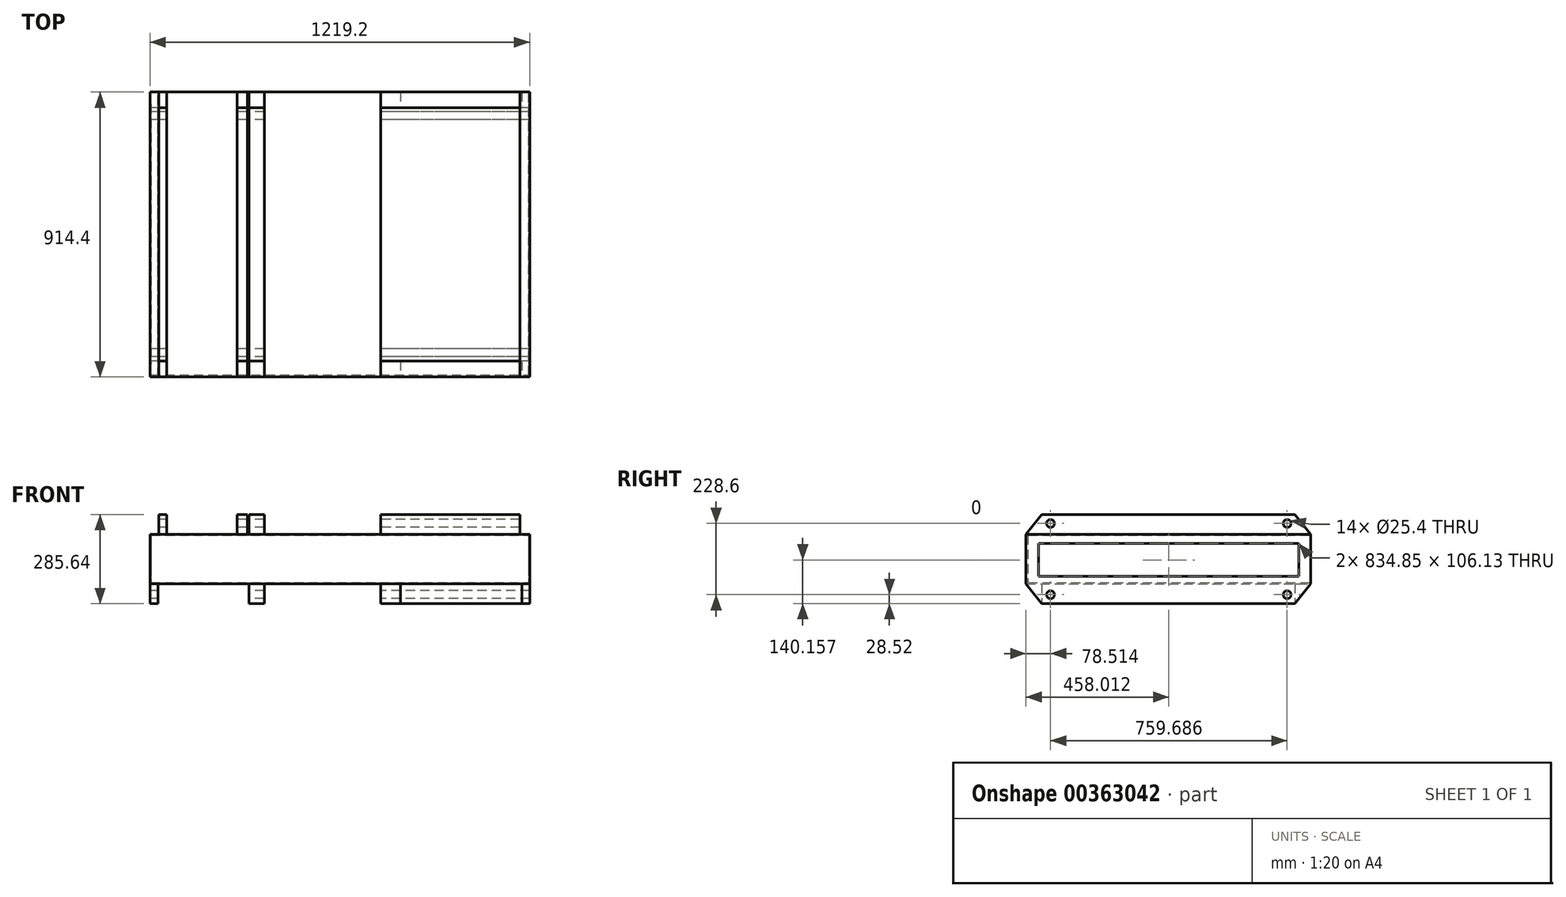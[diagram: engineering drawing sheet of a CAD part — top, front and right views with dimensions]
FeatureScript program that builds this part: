
annotation { "Feature Type Name" : "Feature", "Feature Type Description" : "" }
export const myFeature = defineFeature(function(context is Context, id is Id, definition is map)
    precondition{}
    {
        {
            var Q0;
            Q0=qCreatedBy(makeId("Right.planeOp"),FACE);
            var sketch = newSketch(context, id + "F0", { "sketchPlane" : qUnion([Q0])});
            skLineSegment(sketch, "E0.bottom", {"start": v(457.2, 79.37) * mm, "end": v(-457.2, 79.37) * mm});
            skLineSegment(sketch, "E0.top", {"start": v(457.2, -79.37) * mm, "end": v(-457.2, -79.38) * mm});
            skLineSegment(sketch, "E0.left", {"start": v(457.2, 79.37) * mm, "end": v(457.2, -79.37) * mm});
            skLineSegment(sketch, "E0.right", {"start": v(-457.2, 79.37) * mm, "end": v(-457.2, -79.38) * mm});
            skPoint(sketch, "E0.middle", {"position": v(0, 0) * mm});
            skLineSegment(sketch, "E1", {"start": v(457.2, 79.38) * mm, "end": v(406.4, 142.82) * mm});
            skLineSegment(sketch, "E2", {"start": v(406.4, 142.82) * mm, "end": v(-406.4, 142.82) * mm});
            skLineSegment(sketch, "E3", {"start": v(-406.4, 142.82) * mm, "end": v(-457.2, 79.37) * mm});
            skLineSegment(sketch, "E4", {"start": v(-457.2, -79.38) * mm, "end": v(-406.4, -142.82) * mm});
            skLineSegment(sketch, "E5", {"start": v(-406.4, -142.82) * mm, "end": v(406.4, -142.82) * mm});
            skLineSegment(sketch, "E6", {"start": v(406.4, -142.82) * mm, "end": v(457.2, -79.37) * mm});
            skPoint(sketch, "E7", {"position": v(381, 114.3) * mm});
            skPoint(sketch, "E8", {"position": v(-378.69, 114.3) * mm});
            skPoint(sketch, "E9", {"position": v(381, -114.3) * mm});
            skPoint(sketch, "E10", {"position": v(-378.69, -114.3) * mm});
            skLineSegment(sketch, "E11.bottom", {"start": v(418.24, 50.4) * mm, "end": v(-416.61, 50.4) * mm});
            skLineSegment(sketch, "E11.top", {"start": v(418.24, -55.73) * mm, "end": v(-416.61, -55.73) * mm});
            skLineSegment(sketch, "E11.left", {"start": v(418.24, 50.4) * mm, "end": v(418.24, -55.73) * mm});
            skLineSegment(sketch, "E11.right", {"start": v(-416.61, 50.4) * mm, "end": v(-416.61, -55.73) * mm});
            skSolve(sketch);
        }
        {
            var Q0;
            {var subQ0=sQuery(id+"F0.wireOp",EDGE,"E0.right");Q0=makeQuery(id+"F0.imprint","IMPRINT",FACE,{"disambiguationData":[TD([[makeQuery(id+"F0.imprint","IMPRINT",EDGE,{"derivedFrom":subQ0}),1.0]])]});}
            var Q1;
            {var subQ0=sQuery(id+"F0.wireOp",EDGE,"E0.left");Q1=makeQuery(id+"F0.imprint","IMPRINT",FACE,{"disambiguationData":[TD([[makeQuery(id+"F0.imprint","IMPRINT",EDGE,{"derivedFrom":subQ0}),-1.0]])]});}
            extrude(context, id + "F1", {"entities" : qUnion([Q0, Q1]), "depth" : 1219.2 * mm});
        }
        {
            var Q0;
            {var subQ0=sQuery(id+"F0.wireOp",EDGE,"E1");Q0=makeQuery(id+"F0.imprint","IMPRINT",FACE,{"disambiguationData":[TD([[makeQuery(id+"F0.imprint","IMPRINT",EDGE,{"derivedFrom":subQ0}),1.0]])]});}
            extrude(context, id + "F2", {"entities" : qUnion([Q0]), "operationType" : NewBodyOperationType.ADD, "depth" : 25.4 * mm});
        }
        {
            var Q0;
            {var subQ0=sQuery(id+"F0.wireOp",EDGE,"E4");Q0=makeQuery(id+"F0.imprint","IMPRINT",FACE,{"disambiguationData":[TD([[makeQuery(id+"F0.imprint","IMPRINT",EDGE,{"derivedFrom":subQ0}),1.0]])]});}
            extrude(context, id + "F3", {"entities" : qUnion([Q0]), "operationType" : NewBodyOperationType.ADD, "depth" : 25.4 * mm});
        }
        {
            var Q0;
            Q0=makeQuery(id+"F0.imprint","IMPRINT",FACE,{"disambiguationData":[TD([[makeQuery(id+"F0.imprint","IMPRINT",EDGE,{"derivedFrom":sQuery(id+"F0.wireOp",EDGE,"E0.bottom")}),-1.0]])]});
            extrude(context, id + "F4", {"entities" : qUnion([Q0]), "operationType" : NewBodyOperationType.ADD, "depth" : 1219.2 * mm});
        }
        {
            var Q0;
            Q0=makeQuery(id+"F0.imprint","IMPRINT",FACE,{"disambiguationData":[TD([[makeQuery(id+"F0.imprint","IMPRINT",EDGE,{"derivedFrom":sQuery(id+"F0.wireOp",EDGE,"E0.top")}),1.0]])]});
            extrude(context, id + "F5", {"entities" : qUnion([Q0]), "operationType" : NewBodyOperationType.ADD, "depth" : 1219.2 * mm});
        }
        {
            var Q0;
            Q0=sQuery(id+"F0.wireOp",VERTEX,"E8");
            var Q1;
            Q1=sQuery(id+"F0.wireOp",VERTEX,"E9");
            var Q2;
            Q2=sQuery(id+"F0.wireOp",VERTEX,"E10");
            var Q3;
            Q3=sQuery(id+"F0.wireOp",VERTEX,"E7");
            var Q4;
            Q4=makeQuery(id+"F1.opExtrude","SWEPT_BODY",BODY,{"disambiguationData":[OSD([sQuery(id+"F0.wireOp",EDGE,"E0.bottom"),sQuery(id+"F0.wireOp",EDGE,"E0.top"),sQuery(id+"F0.wireOp",EDGE,"E0.left"),sQuery(id+"F0.wireOp",EDGE,"E0.right")])]});
            hole(context, id + "F6", {"style" : HoleStyle.SIMPLE, "endStyle" : HoleEndStyle.THROUGH, "oppositeDirection" : true, "holeDiameter" : 25.4 * mm, "isTappedThrough" : true, "tappedDepth" : 12.7 * mm, "tapClearance" : 3, "startFromSketch" : true, "locations" : qUnion([Q0, Q1, Q2, Q3]), "scope" : qUnion([Q4])});
        }
        {
            var Q0;
            {var subQ0=sQuery(id+"F0.wireOp",EDGE,"E5");Q0=makeQuery(id+"F5.boolean.opBoolean","MERGE",FACE,{"derivedFrom":[makeQuery(id+"F3.opExtrude","SWEPT_FACE",FACE,{"disambiguationData":[OSD([subQ0])]}),makeQuery(id+"F5.opExtrude","SWEPT_FACE",FACE,{"disambiguationData":[OSD([subQ0])]})]});}
            var sketch = newSketch(context, id + "F7", { "sketchPlane" : qUnion([Q0])});
            skLineSegment(sketch, "E12.bottom", {"start": v(25.4, 551.74) * mm, "end": v(1193.8, 551.74) * mm});
            skLineSegment(sketch, "E12.top", {"start": v(25.4, -593.28) * mm, "end": v(1193.8, -593.28) * mm});
            skLineSegment(sketch, "E12.left", {"start": v(25.4, 551.74) * mm, "end": v(25.4, -593.28) * mm});
            skLineSegment(sketch, "E12.right", {"start": v(1193.8, 551.74) * mm, "end": v(1193.8, -593.28) * mm});
            skLineSegment(sketch, "E13.bottom", {"start": v(1219.2, 23.88) * mm, "end": v(1193.8, 23.88) * mm});
            skLineSegment(sketch, "E13.top", {"start": v(1219.2, -593.28) * mm, "end": v(1193.8, -593.28) * mm});
            skLineSegment(sketch, "E13.left", {"start": v(1219.2, 23.88) * mm, "end": v(1219.2, -593.28) * mm});
            skLineSegment(sketch, "E13.right", {"start": v(1193.8, 23.88) * mm, "end": v(1193.8, -593.28) * mm});
            skLineSegment(sketch, "E14.top", {"start": v(1219.2, 551.74) * mm, "end": v(1193.8, 551.74) * mm});
            skLineSegment(sketch, "E14.left", {"start": v(1219.2, 23.88) * mm, "end": v(1219.2, 551.74) * mm});
            skLineSegment(sketch, "E14.right", {"start": v(1193.8, 23.88) * mm, "end": v(1193.8, 551.74) * mm});
            skPoint(sketch, "E15.oppositeSnap0", {"position": v(0, 0) * mm});
            skLineSegment(sketch, "E15.bottom", {"start": v(25.4, 551.74) * mm, "end": v(0, 551.74) * mm});
            skLineSegment(sketch, "E15.top", {"start": v(25.4, -593.28) * mm, "end": v(0, -593.28) * mm});
            skLineSegment(sketch, "E15.right", {"start": v(0, 551.74) * mm, "end": v(0, -593.28) * mm});
            skLineSegment(sketch, "E16.bottom", {"start": v(318.15, 551.74) * mm, "end": v(367.07, 551.74) * mm});
            skLineSegment(sketch, "E16.top", {"start": v(318.15, -593.28) * mm, "end": v(367.07, -593.28) * mm});
            skLineSegment(sketch, "E16.left", {"start": v(318.15, 551.74) * mm, "end": v(318.15, -593.28) * mm});
            skLineSegment(sketch, "E16.right", {"start": v(367.07, 551.74) * mm, "end": v(367.07, -593.28) * mm});
            skLineSegment(sketch, "E17.bottom", {"start": v(740.44, 551.74) * mm, "end": v(804.81, 551.74) * mm});
            skLineSegment(sketch, "E17.top", {"start": v(740.44, -593.28) * mm, "end": v(804.81, -593.28) * mm});
            skLineSegment(sketch, "E17.left", {"start": v(740.44, 551.74) * mm, "end": v(740.44, -593.28) * mm});
            skLineSegment(sketch, "E17.right", {"start": v(804.81, 551.74) * mm, "end": v(804.81, -593.28) * mm});
            skSolve(sketch);
        }
        {
            var Q0;
            {var subQ0=sQuery(id+"F7.wireOp",EDGE,"E14.right");var subQ7=sQuery(id+"F7.wireOp",EDGE,"E13.right");var subQ8=makeQuery(id+"F7.imprint","INTERSECT",VERTEX,{"derivedFrom":[subQ7,sQuery(id+"F7.wireOp",EDGE,"E13.bottom"),subQ0]});Q0=makeQuery(id+"F7.imprint","IMPRINT",FACE,{"disambiguationData":[TD([[makeQuery(id+"F7.imprint","IMPRINT",EDGE,{"disambiguationData":[TD([[subQ8,-1.0]])],"derivedFrom":subQ7}),-1.0]])]});}
            var Q1;
            {var subQ0=sQuery(id+"F7.wireOp",EDGE,"E13.right");var subQ1=sQuery(id+"F7.wireOp",EDGE,"E12.top");var subQ2=makeQuery(id+"F7.imprint","INTERSECT",VERTEX,{"derivedFrom":[subQ1,sQuery(id+"F7.wireOp",EDGE,"E13.top"),subQ0]});Q1=makeQuery(id+"F7.imprint","IMPRINT",FACE,{"disambiguationData":[TD([[makeQuery(id+"F7.imprint","IMPRINT",EDGE,{"disambiguationData":[TD([[subQ2,1.0]])],"derivedFrom":subQ1}),1.0]])]});}
            var Q2;
            {var subQ0=sQuery(id+"F7.wireOp",EDGE,"E16.right");var subQ1=sQuery(id+"F7.wireOp",EDGE,"E12.top");var subQ2=makeQuery(id+"F7.imprint","INTERSECT",VERTEX,{"derivedFrom":[subQ1,sQuery(id+"F7.wireOp",EDGE,"E16.top"),subQ0]});Q2=makeQuery(id+"F7.imprint","IMPRINT",FACE,{"disambiguationData":[TD([[makeQuery(id+"F7.imprint","IMPRINT",EDGE,{"disambiguationData":[TD([[subQ2,-1.0]])],"derivedFrom":subQ1}),1.0]])]});}
            var Q3;
            {var subQ0=sQuery(id+"F7.wireOp",EDGE,"E16.right");var subQ1=sQuery(id+"F0.wireOp",EDGE,"E5");var subQ2=sQuery(id+"F0.wireOp",EDGE,"E4");var subQ3=makeQuery(id+"F5.boolean.opBoolean","MERGE",EDGE,{"derivedFrom":[makeQuery(id+"F3.opExtrude","SWEPT_EDGE",EDGE,{"disambiguationData":[OSD([subQ2,subQ1])]}),makeQuery(id+"F5.opExtrude","SWEPT_EDGE",EDGE,{"disambiguationData":[OSD([subQ2,subQ1])]})]});var subQ4=makeQuery(id+"F7.imprint","INTERSECT",VERTEX,{"derivedFrom":[subQ3,subQ0]});Q3=makeQuery(id+"F7.imprint","IMPRINT",FACE,{"disambiguationData":[TD([[makeQuery(id+"F7.imprint","IMPRINT",EDGE,{"disambiguationData":[TD([[subQ4,-1.0]])],"derivedFrom":subQ0}),1.0]])]});}
            var Q4;
            {var subQ0=sQuery(id+"F7.wireOp",EDGE,"E12.left");var subQ1=sQuery(id+"F0.wireOp",EDGE,"E5");var subQ2=sQuery(id+"F0.wireOp",EDGE,"E4");var subQ3=makeQuery(id+"F5.boolean.opBoolean","MERGE",EDGE,{"derivedFrom":[makeQuery(id+"F3.opExtrude","SWEPT_EDGE",EDGE,{"disambiguationData":[OSD([subQ2,subQ1])]}),makeQuery(id+"F5.opExtrude","SWEPT_EDGE",EDGE,{"disambiguationData":[OSD([subQ2,subQ1])]})]});var subQ4=makeQuery(id+"F7.imprint","INTERSECT",VERTEX,{"derivedFrom":[subQ3,subQ0]});Q4=makeQuery(id+"F7.imprint","IMPRINT",FACE,{"disambiguationData":[TD([[makeQuery(id+"F7.imprint","IMPRINT",EDGE,{"disambiguationData":[TD([[subQ4,-1.0]])],"derivedFrom":subQ0}),1.0]])]});}
            var Q5;
            {var subQ0=sQuery(id+"F7.wireOp",EDGE,"E12.left");var subQ1=sQuery(id+"F7.wireOp",EDGE,"E12.top");var subQ2=makeQuery(id+"F7.imprint","INTERSECT",VERTEX,{"derivedFrom":[subQ1,sQuery(id+"F7.wireOp",EDGE,"E15.top"),subQ0]});Q5=makeQuery(id+"F7.imprint","IMPRINT",FACE,{"disambiguationData":[TD([[makeQuery(id+"F7.imprint","IMPRINT",EDGE,{"disambiguationData":[TD([[subQ2,-1.0]])],"derivedFrom":subQ1}),1.0]])]});}
            var Q6;
            {var subQ0=sQuery(id+"F7.wireOp",EDGE,"E14.right");var subQ1=sQuery(id+"F7.wireOp",EDGE,"E12.bottom");var subQ2=makeQuery(id+"F7.imprint","INTERSECT",VERTEX,{"derivedFrom":[subQ1,sQuery(id+"F7.wireOp",EDGE,"E14.top"),subQ0]});Q6=makeQuery(id+"F7.imprint","IMPRINT",FACE,{"disambiguationData":[TD([[makeQuery(id+"F7.imprint","IMPRINT",EDGE,{"disambiguationData":[TD([[subQ2,1.0]])],"derivedFrom":subQ1}),-1.0]])]});}
            var Q7;
            {var subQ0=sQuery(id+"F7.wireOp",EDGE,"E16.right");var subQ1=sQuery(id+"F7.wireOp",EDGE,"E12.bottom");var subQ2=makeQuery(id+"F7.imprint","INTERSECT",VERTEX,{"derivedFrom":[subQ1,sQuery(id+"F7.wireOp",EDGE,"E16.bottom"),subQ0]});Q7=makeQuery(id+"F7.imprint","IMPRINT",FACE,{"disambiguationData":[TD([[makeQuery(id+"F7.imprint","IMPRINT",EDGE,{"disambiguationData":[TD([[subQ2,-1.0]])],"derivedFrom":subQ1}),-1.0]])]});}
            var Q8;
            {var subQ0=sQuery(id+"F7.wireOp",EDGE,"E12.left");var subQ1=sQuery(id+"F7.wireOp",EDGE,"E12.bottom");var subQ2=makeQuery(id+"F7.imprint","INTERSECT",VERTEX,{"derivedFrom":[subQ1,sQuery(id+"F7.wireOp",EDGE,"E15.bottom"),subQ0]});Q8=makeQuery(id+"F7.imprint","IMPRINT",FACE,{"disambiguationData":[TD([[makeQuery(id+"F7.imprint","IMPRINT",EDGE,{"disambiguationData":[TD([[subQ2,-1.0]])],"derivedFrom":subQ1}),-1.0]])]});}
            extrude(context, id + "F8", {"entities" : qUnion([Q0, Q1, Q2, Q3, Q4, Q5, Q6, Q7, Q8]), "operationType" : NewBodyOperationType.REMOVE, "oppositeDirection" : true, "depth" : 63.5 * mm});
        }
        {
            var Q0;
            Q0=makeQuery(id+"F1.opExtrude","SWEPT_FACE",FACE,{"disambiguationData":[OSD([sQuery(id+"F0.wireOp",EDGE,"E0.left")])]});
            var sketch = newSketch(context, id + "F9", { "sketchPlane" : qUnion([Q0])});
            skLineSegment(sketch, "E18.bottom", {"start": v(-1219.2, 79.37) * mm, "end": v(0, 79.37) * mm});
            skLineSegment(sketch, "E18.top", {"start": v(-1219.2, -79.38) * mm, "end": v(0, -79.38) * mm});
            skLineSegment(sketch, "E18.left", {"start": v(-1219.2, 79.37) * mm, "end": v(-1219.2, -79.38) * mm});
            skLineSegment(sketch, "E18.right", {"start": v(0, 79.37) * mm, "end": v(0, -79.38) * mm});
            skLineSegment(sketch, "E19.bottom", {"start": v(11.99, 76.2) * mm, "end": v(-1241.76, 76.2) * mm});
            skLineSegment(sketch, "E19.top", {"start": v(11.99, -76.2) * mm, "end": v(-1241.76, -76.2) * mm});
            skLineSegment(sketch, "E19.left", {"start": v(11.99, 76.2) * mm, "end": v(11.99, -76.2) * mm});
            skLineSegment(sketch, "E19.right", {"start": v(-1241.76, 76.2) * mm, "end": v(-1241.76, -76.2) * mm});
            skLineSegment(sketch, "E20.bottom", {"start": v(-1247.32, -79.38) * mm, "end": v(48.41, -79.38) * mm});
            skLineSegment(sketch, "E20.top", {"start": v(-1247.32, 79.37) * mm, "end": v(48.41, 79.37) * mm});
            skLineSegment(sketch, "E20.left", {"start": v(-1247.32, -79.38) * mm, "end": v(-1247.32, 79.37) * mm});
            skLineSegment(sketch, "E20.right", {"start": v(48.41, -79.38) * mm, "end": v(48.41, 79.37) * mm});
            skLineSegment(sketch, "E21.bottom", {"start": v(11.99, 76.2) * mm, "end": v(0, 76.2) * mm});
            skLineSegment(sketch, "E21.top", {"start": v(11.99, 89.74) * mm, "end": v(0, 89.74) * mm});
            skLineSegment(sketch, "E21.left", {"start": v(11.99, 76.2) * mm, "end": v(11.99, 89.74) * mm});
            skLineSegment(sketch, "E21.right", {"start": v(0, 76.2) * mm, "end": v(0, 89.74) * mm});
            skLineSegment(sketch, "E22.bottom", {"start": v(11.99, -76.2) * mm, "end": v(48.41, -76.2) * mm});
            skLineSegment(sketch, "E22.top", {"start": v(11.99, -79.38) * mm, "end": v(48.41, -79.38) * mm});
            skLineSegment(sketch, "E22.left", {"start": v(11.99, -76.2) * mm, "end": v(11.99, -79.38) * mm});
            skLineSegment(sketch, "E22.right", {"start": v(48.41, -76.2) * mm, "end": v(48.41, -79.38) * mm});
            skLineSegment(sketch, "E23.bottom", {"start": v(0, 76.2) * mm, "end": v(-3.18, 76.2) * mm});
            skLineSegment(sketch, "E23.top", {"start": v(0, -76.2) * mm, "end": v(-3.17, -76.2) * mm});
            skLineSegment(sketch, "E23.left", {"start": v(0, 76.2) * mm, "end": v(0, -76.2) * mm});
            skLineSegment(sketch, "E23.right", {"start": v(-3.18, 76.2) * mm, "end": v(-3.17, -76.2) * mm});
            skLineSegment(sketch, "E24.bottom", {"start": v(-1219.2, 76.2) * mm, "end": v(-1216.03, 76.2) * mm});
            skLineSegment(sketch, "E24.top", {"start": v(-1219.2, -76.2) * mm, "end": v(-1216.03, -76.2) * mm});
            skLineSegment(sketch, "E24.left", {"start": v(-1219.2, 76.2) * mm, "end": v(-1219.2, -76.2) * mm});
            skLineSegment(sketch, "E24.right", {"start": v(-1216.03, 76.2) * mm, "end": v(-1216.03, -76.2) * mm});
            skLineSegment(sketch, "E25.bottom", {"start": v(0, 79.37) * mm, "end": v(-3.18, 79.37) * mm});
            skLineSegment(sketch, "E25.left", {"start": v(0, 79.37) * mm, "end": v(0, 76.2) * mm});
            skLineSegment(sketch, "E25.right", {"start": v(-3.18, 79.37) * mm, "end": v(-3.18, 76.2) * mm});
            skSolve(sketch);
        }
        {
            var Q0;
            {var subQ0=sQuery(id+"F9.wireOp",EDGE,"E23.right");Q0=makeQuery(id+"F9.imprint","IMPRINT",FACE,{"disambiguationData":[TD([[makeQuery(id+"F9.imprint","IMPRINT",EDGE,{"derivedFrom":subQ0}),-1.0]])]});}
            extrude(context, id + "F10", {"entities" : qUnion([Q0]), "operationType" : NewBodyOperationType.REMOVE, "oppositeDirection" : true, "depth" : 908.05 * mm});
        }
        {
            var Q0;
            {var subQ0=sQuery(id+"F9.wireOp",EDGE,"E23.right");Q0=makeQuery(id+"F9.imprint","IMPRINT",FACE,{"disambiguationData":[TD([[makeQuery(id+"F9.imprint","IMPRINT",EDGE,{"derivedFrom":subQ0}),-1.0]])]});}
            extrude(context, id + "F11", {"entities" : qUnion([Q0]), "operationType" : NewBodyOperationType.REMOVE, "oppositeDirection" : true, "depth" : 889 * mm});
        }
        {
            var Q0;
            Q0=makeQuery(id+"F1.opExtrude","SWEPT_FACE",FACE,{"disambiguationData":[OSD([sQuery(id+"F0.wireOp",EDGE,"E0.right")])]});
            var sketch = newSketch(context, id + "F12", { "sketchPlane" : qUnion([Q0])});
            skLineSegment(sketch, "E26", {"start": v(28.57, 79.37) * mm, "end": v(28.57, 142.31) * mm});
            skLineSegment(sketch, "E27.bottom", {"start": v(28.58, 79.37) * mm, "end": v(279.4, 79.37) * mm});
            skLineSegment(sketch, "E27.top", {"start": v(28.57, 145.91) * mm, "end": v(279.4, 145.91) * mm});
            skLineSegment(sketch, "E27.left", {"start": v(28.58, 79.37) * mm, "end": v(28.57, 145.91) * mm});
            skLineSegment(sketch, "E27.right", {"start": v(279.4, 79.37) * mm, "end": v(279.4, 145.91) * mm});
            skLineSegment(sketch, "E28.top", {"start": v(322.89, 79.37) * mm, "end": v(325.77, 79.37) * mm});
            skLineSegment(sketch, "E29.bottom", {"start": v(318.15, -79.32) * mm, "end": v(367.46, -79.32) * mm});
            skLineSegment(sketch, "E29.top", {"start": v(318.15, 186.17) * mm, "end": v(367.46, 186.17) * mm});
            skLineSegment(sketch, "E29.left", {"start": v(318.15, -79.32) * mm, "end": v(318.15, 186.17) * mm});
            skLineSegment(sketch, "E29.right", {"start": v(367.46, -79.32) * mm, "end": v(367.46, 186.17) * mm});
            skLineSegment(sketch, "E30.bottom", {"start": v(740.44, -79.32) * mm, "end": v(804.81, -79.32) * mm});
            skLineSegment(sketch, "E30.top", {"start": v(740.44, 186.17) * mm, "end": v(804.81, 186.17) * mm});
            skLineSegment(sketch, "E30.left", {"start": v(740.44, -79.32) * mm, "end": v(740.44, 186.17) * mm});
            skLineSegment(sketch, "E30.right", {"start": v(804.81, -79.32) * mm, "end": v(804.81, 186.17) * mm});
            skLineSegment(sketch, "E31.bottom", {"start": v(313.2, 145.91) * mm, "end": v(370.35, 145.91) * mm});
            skLineSegment(sketch, "E31.top", {"start": v(313.2, 79.37) * mm, "end": v(370.35, 79.37) * mm});
            skLineSegment(sketch, "E31.left", {"start": v(313.2, 145.91) * mm, "end": v(313.2, 79.37) * mm});
            skLineSegment(sketch, "E31.right", {"start": v(370.35, 145.91) * mm, "end": v(370.35, 79.37) * mm});
            skLineSegment(sketch, "E32.bottom", {"start": v(740.44, 79.38) * mm, "end": v(736.5, 79.38) * mm});
            skLineSegment(sketch, "E32.top", {"start": v(740.44, 201.6) * mm, "end": v(736.5, 201.6) * mm});
            skLineSegment(sketch, "E32.left", {"start": v(740.44, 79.38) * mm, "end": v(740.44, 201.6) * mm});
            skLineSegment(sketch, "E32.right", {"start": v(736.5, 79.38) * mm, "end": v(736.5, 201.6) * mm});
            skLineSegment(sketch, "E33.bottom", {"start": v(804.81, 79.37) * mm, "end": v(1160.9, 79.37) * mm});
            skLineSegment(sketch, "E33.top", {"start": v(804.81, 167.9) * mm, "end": v(1160.9, 167.9) * mm});
            skLineSegment(sketch, "E33.left", {"start": v(804.81, 79.37) * mm, "end": v(804.81, 167.9) * mm});
            skLineSegment(sketch, "E33.right", {"start": v(1160.9, 79.37) * mm, "end": v(1160.9, 167.9) * mm});
            skLineSegment(sketch, "E34.bottom", {"start": v(1219.2, 167.9) * mm, "end": v(1187.45, 167.9) * mm});
            skLineSegment(sketch, "E34.top", {"start": v(1219.2, 79.37) * mm, "end": v(1187.45, 79.37) * mm});
            skLineSegment(sketch, "E34.left", {"start": v(1219.2, 167.9) * mm, "end": v(1219.2, 79.37) * mm});
            skLineSegment(sketch, "E34.right", {"start": v(1187.45, 167.9) * mm, "end": v(1187.45, 79.37) * mm});
            skLineSegment(sketch, "E35.bottom", {"start": v(1187.45, 167.9) * mm, "end": v(1160.9, 167.9) * mm});
            skLineSegment(sketch, "E35.top", {"start": v(1187.45, 79.37) * mm, "end": v(1160.9, 79.37) * mm});
            skLineSegment(sketch, "E35.right", {"start": v(1160.9, 167.9) * mm, "end": v(1160.9, 79.37) * mm});
            skLineSegment(sketch, "E36.bottom", {"start": v(809.73, 79.37) * mm, "end": v(835.13, 79.37) * mm});
            skLineSegment(sketch, "E36.top", {"start": v(809.73, 159.77) * mm, "end": v(835.13, 159.77) * mm});
            skLineSegment(sketch, "E36.left", {"start": v(809.73, 79.37) * mm, "end": v(809.73, 159.77) * mm});
            skLineSegment(sketch, "E36.right", {"start": v(835.13, 79.37) * mm, "end": v(835.13, 159.77) * mm});
            skPoint(sketch, "E37.oppositeSnap0", {"position": v(772.62, 186.17) * mm});
            skLineSegment(sketch, "E37.bottom", {"start": v(313.2, 79.37) * mm, "end": v(809.6, 79.37) * mm});
            skLineSegment(sketch, "E37.top", {"start": v(313.2, 186.17) * mm, "end": v(809.6, 186.17) * mm});
            skLineSegment(sketch, "E37.left", {"start": v(313.2, 79.37) * mm, "end": v(313.2, 186.17) * mm});
            skLineSegment(sketch, "E37.right", {"start": v(809.6, 79.37) * mm, "end": v(809.6, 186.17) * mm});
            skLineSegment(sketch, "E38.bottom", {"start": v(28.57, 145.91) * mm, "end": v(0, 145.91) * mm});
            skLineSegment(sketch, "E38.top", {"start": v(28.58, 79.37) * mm, "end": v(0, 79.37) * mm});
            skLineSegment(sketch, "E38.left", {"start": v(28.57, 145.91) * mm, "end": v(28.58, 79.37) * mm});
            skLineSegment(sketch, "E38.right", {"start": v(0, 145.91) * mm, "end": v(0, 79.37) * mm});
            skLineSegment(sketch, "E39.bottom", {"start": v(53.97, 145.91) * mm, "end": v(28.57, 145.91) * mm});
            skLineSegment(sketch, "E39.top", {"start": v(53.98, 79.37) * mm, "end": v(28.58, 79.37) * mm});
            skLineSegment(sketch, "E39.left", {"start": v(53.97, 145.91) * mm, "end": v(53.98, 79.37) * mm});
            skSolve(sketch);
        }
        {
            var Q0;
            {var subQ0=sQuery(id+"F12.wireOp",EDGE,"E35.right");Q0=makeQuery(id+"F12.imprint","IMPRINT",FACE,{"disambiguationData":[TD([[makeQuery(id+"F12.imprint","IMPRINT",EDGE,{"derivedFrom":subQ0}),-1.0]])]});}
            var Q1;
            {var subQ0=sQuery(id+"F12.wireOp",EDGE,"E33.left");Q1=makeQuery(id+"F12.imprint","IMPRINT",FACE,{"disambiguationData":[TD([[makeQuery(id+"F12.imprint","IMPRINT",EDGE,{"derivedFrom":subQ0}),-1.0]])]});}
            var Q2;
            {var subQ3=sQuery(id+"F12.wireOp",EDGE,"E33.left");Q2=makeQuery(id+"F12.imprint","IMPRINT",FACE,{"disambiguationData":[TD([[makeQuery(id+"F12.imprint","IMPRINT",EDGE,{"derivedFrom":subQ3}),1.0]])]});}
            var Q3;
            {var subQ0=sQuery(id+"F12.wireOp",EDGE,"E37.bottom");var subQ5=sQuery(id+"F12.wireOp",EDGE,"E32.right");var subQ6=makeQuery(id+"F12.imprint","INTERSECT",VERTEX,{"derivedFrom":[subQ5,subQ0]});Q3=makeQuery(id+"F12.imprint","IMPRINT",FACE,{"disambiguationData":[TD([[makeQuery(id+"F12.imprint","IMPRINT",EDGE,{"disambiguationData":[TD([[subQ6,-1.0]])],"derivedFrom":subQ5}),-1.0]])]});}
            var Q4;
            {var subQ0=sQuery(id+"F12.wireOp",EDGE,"E37.bottom");var subQ1=makeQuery(id+"F12.imprint","IMPRINT",VERTEX,{"disambiguationData":[OD(0.0)],"derivedFrom":subQ0});Q4=makeQuery(id+"F12.imprint","IMPRINT",FACE,{"disambiguationData":[TD([[makeQuery(id+"F12.imprint","IMPRINT",EDGE,{"disambiguationData":[TD([[subQ1,-1.0]])],"derivedFrom":subQ0}),-1.0]])]});}
            var Q5;
            {var subQ0=sQuery(id+"F12.wireOp",EDGE,"E31.right");Q5=makeQuery(id+"F12.imprint","IMPRINT",FACE,{"disambiguationData":[TD([[makeQuery(id+"F12.imprint","IMPRINT",EDGE,{"derivedFrom":subQ0}),1.0]])]});}
            var Q6;
            {var subQ5=sQuery(id+"F12.wireOp",EDGE,"E31.right");Q6=makeQuery(id+"F12.imprint","IMPRINT",FACE,{"disambiguationData":[TD([[makeQuery(id+"F12.imprint","IMPRINT",EDGE,{"derivedFrom":subQ5}),-1.0]])]});}
            var Q7;
            {var subQ0=sQuery(id+"F12.wireOp",EDGE,"E37.bottom");var subQ1=sQuery(id+"F12.wireOp",EDGE,"E29.left");var subQ2=makeQuery(id+"F12.imprint","INTERSECT",VERTEX,{"derivedFrom":[subQ1,subQ0]});Q7=makeQuery(id+"F12.imprint","IMPRINT",FACE,{"disambiguationData":[TD([[makeQuery(id+"F12.imprint","IMPRINT",EDGE,{"disambiguationData":[TD([[subQ2,-1.0]])],"derivedFrom":subQ1}),1.0]])]});}
            var Q8;
            {var subQ0=sQuery(id+"F12.wireOp",EDGE,"E27.bottom");Q8=makeQuery(id+"F12.imprint","IMPRINT",FACE,{"disambiguationData":[TD([[makeQuery(id+"F12.imprint","IMPRINT",EDGE,{"derivedFrom":subQ0}),-1.0]])]});}
            var Q9;
            {var subQ0=sQuery(id+"F12.wireOp",EDGE,"E37.top");var subQ1=sQuery(id+"F12.wireOp",EDGE,"E29.left");var subQ2=makeQuery(id+"F12.imprint","INTERSECT",VERTEX,{"derivedFrom":[subQ1,subQ0]});Q9=makeQuery(id+"F12.imprint","IMPRINT",FACE,{"disambiguationData":[TD([[makeQuery(id+"F12.imprint","IMPRINT",EDGE,{"disambiguationData":[TD([[subQ2,1.0]])],"derivedFrom":subQ1}),-1.0]])]});}
            var Q10;
            {var subQ0=sQuery(id+"F12.wireOp",EDGE,"E37.top");var subQ1=sQuery(id+"F12.wireOp",EDGE,"E29.left");var subQ2=makeQuery(id+"F12.imprint","INTERSECT",VERTEX,{"derivedFrom":[subQ1,subQ0]});Q10=makeQuery(id+"F12.imprint","IMPRINT",FACE,{"disambiguationData":[TD([[makeQuery(id+"F12.imprint","IMPRINT",EDGE,{"disambiguationData":[TD([[subQ2,1.0]])],"derivedFrom":subQ1}),1.0]])]});}
            var Q11;
            Q11=makeQuery(id+"F12.imprint","IMPRINT",FACE,{"disambiguationData":[TD([[makeQuery(id+"F12.imprint","IMPRINT",EDGE,{"derivedFrom":sQuery(id+"F12.wireOp",EDGE,"E34.bottom")}),1.0]])]});
            var Q12;
            {var subQ1=sQuery(id+"F12.wireOp",EDGE,"E38.bottom");Q12=makeQuery(id+"F12.imprint","IMPRINT",FACE,{"disambiguationData":[TD([[makeQuery(id+"F12.imprint","IMPRINT",EDGE,{"derivedFrom":subQ1}),1.0]])]});}
            extrude(context, id + "F13", {"entities" : qUnion([Q0, Q1, Q2, Q3, Q4, Q5, Q6, Q7, Q8, Q9, Q10, Q11, Q12]), "operationType" : NewBodyOperationType.REMOVE, "oppositeDirection" : true, "depth" : 1016 * mm});
        }
    });
